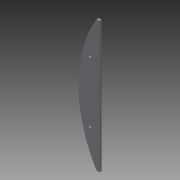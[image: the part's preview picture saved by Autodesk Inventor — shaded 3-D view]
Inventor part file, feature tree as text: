
AUTODESK INVENTOR PART (.ipt)
format: ipt  version: 2015 (Build 190159000, 159)  size: 81,408 bytes
history: native  units: mm
features: extrude x2, sketch x1
ambient origin geometry x8: Origin, YZ Plane, XZ Plane, XY Plane, X Axis, Y Axis, Z Axis, Center Point
bodies: Solid1 (feature_tree)
feature tree (3):
  sketch  "Sketch1"  dims[d2=3.0mm d3=3.0mm d11=2.0mm d12=0.0mm d13=35.0mm d14=35.35mm d17=3.0mm d21=3.0mm d22=2.0mm d23=0.0mm]
  extrude  "Extrusion1"  Depth=2.0mm
  extrude  "Extrusion3"  Depth=2.0mm TaperAngle=0.0deg
